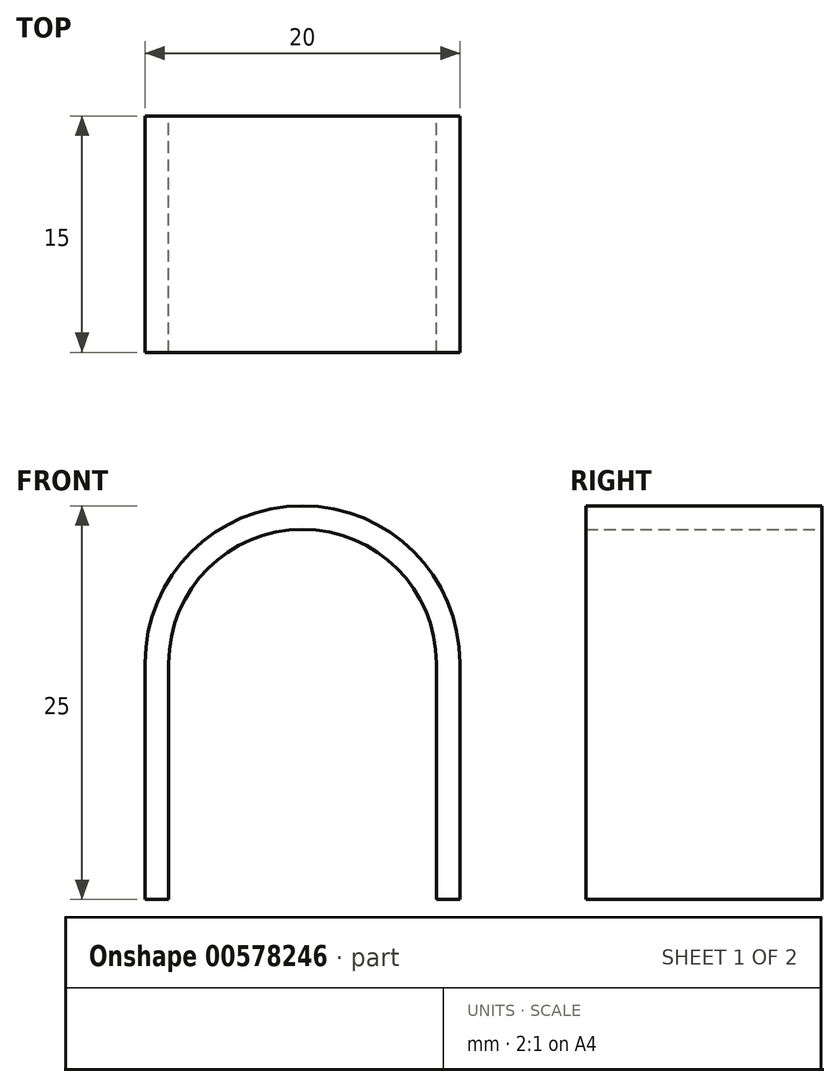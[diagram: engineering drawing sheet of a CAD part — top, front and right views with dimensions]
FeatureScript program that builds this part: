
annotation { "Feature Type Name" : "Feature", "Feature Type Description" : "" }
export const myFeature = defineFeature(function(context is Context, id is Id, definition is map)
    precondition{}
    {
        {
            var Q0;
            Q0=qCreatedBy(makeId("Front.planeOp"),FACE);
            var sketch = newSketch(context, id + "F0", { "sketchPlane" : qUnion([Q0])});
            skArc(sketch, "E0", {"start": v(10, 0) * mm, "mid": v(0, 10) * mm, "end": v(-10, 0) * mm});
            skArc(sketch, "E1", {"start": v(8.5, 0) * mm, "mid": v(0, 8.5) * mm, "end": v(-8.5, 0) * mm});
            skLineSegment(sketch, "E2", {"start": v(-10, 0) * mm, "end": v(-10, -15) * mm});
            skLineSegment(sketch, "E3", {"start": v(10, 0) * mm, "end": v(10, -15) * mm});
            skLineSegment(sketch, "E4", {"start": v(-8.5, 0) * mm, "end": v(-8.5, -15) * mm});
            skLineSegment(sketch, "E5", {"start": v(-8.5, -15) * mm, "end": v(-10, -15) * mm});
            skLineSegment(sketch, "E6", {"start": v(8.5, 0) * mm, "end": v(8.5, -15) * mm});
            skLineSegment(sketch, "E7", {"start": v(8.5, -15) * mm, "end": v(10, -15) * mm});
            skSolve(sketch);
        }
        {
            var Q0;
            Q0=makeQuery(id+"F0.imprint","IMPRINT",FACE,{"disambiguationData":[TD([[makeQuery(id+"F0.imprint","IMPRINT",EDGE,{"derivedFrom":sQuery(id+"F0.wireOp",EDGE,"E0")}),1.0]])]});
            extrude(context, id + "F1", {"entities" : qUnion([Q0]), "depth" : 15 * mm, "offsetDistance" : 25 * mm});
        }
    });
